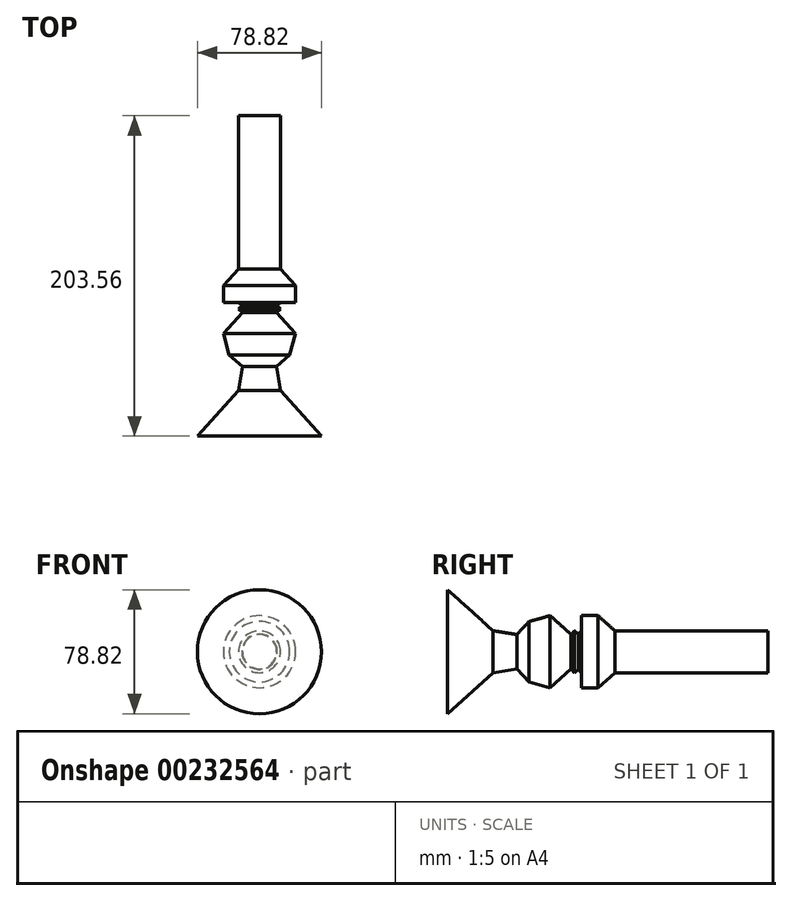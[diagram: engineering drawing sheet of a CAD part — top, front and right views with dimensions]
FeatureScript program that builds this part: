
annotation { "Feature Type Name" : "Feature", "Feature Type Description" : "" }
export const myFeature = defineFeature(function(context is Context, id is Id, definition is map)
    precondition{}
    {
        {
            var Q0;
            Q0=qCreatedBy(makeId("Top.planeOp"),FACE);
            var sketch = newSketch(context, id + "F0", { "sketchPlane" : qUnion([Q0])});
            skLineSegment(sketch, "E0", {"start": v(0, 54.64) * mm, "end": v(-13.33, 54.64) * mm});
            skLineSegment(sketch, "E1", {"start": v(-22.92, 43.98) * mm, "end": v(-13.33, 54.64) * mm});
            skLineSegment(sketch, "E2", {"start": v(-22.92, 43.98) * mm, "end": v(-22.92, 33.32) * mm});
            skLineSegment(sketch, "E3", {"start": v(-13.33, 33.32) * mm, "end": v(-11.2, 31.4) * mm});
            skLineSegment(sketch, "E4", {"start": v(-11.2, 31.4) * mm, "end": v(-13.33, 29.05) * mm});
            skLineSegment(sketch, "E5", {"start": v(-13.33, 29.05) * mm, "end": v(-10.91, 26.88) * mm});
            skLineSegment(sketch, "E6", {"start": v(-10.91, 26.88) * mm, "end": v(-13.33, 24.2) * mm});
            skLineSegment(sketch, "E7", {"start": v(-13.33, 24.2) * mm, "end": v(-22.92, 13.53) * mm});
            skLineSegment(sketch, "E8", {"start": v(-22.92, 13.53) * mm, "end": v(-19.2, 0) * mm});
            skLineSegment(sketch, "E9", {"start": v(-19.2, 0) * mm, "end": v(-10.91, -7.45) * mm});
            skLineSegment(sketch, "E10", {"start": v(-10.91, -7.45) * mm, "end": v(-13.33, -22.66) * mm});
            skLineSegment(sketch, "E11", {"start": v(-13.33, -22.66) * mm, "end": v(-22.92, -33.32) * mm});
            skLineSegment(sketch, "E12", {"start": v(-22.92, -33.32) * mm, "end": v(-39.4, -51.64) * mm});
            skLineSegment(sketch, "E13", {"start": v(-39.4, -51.64) * mm, "end": v(0, -51.64) * mm});
            skLineSegment(sketch, "E14", {"start": v(-22.92, 33.32) * mm, "end": v(-13.33, 33.32) * mm});
            skLineSegment(sketch, "E15", {"start": v(0, 54.64) * mm, "end": v(0, -51.64) * mm});
            skSolve(sketch);
        }
        {
            var Q0;
            Q0=makeQuery(id+"F0.imprint","IMPRINT",FACE,{"disambiguationData":[TD([[makeQuery(id+"F0.imprint","IMPRINT",EDGE,{"derivedFrom":sQuery(id+"F0.wireOp",EDGE,"E0")}),1.0]])]});
            var Q1;
            Q1=sQuery(id+"F0.wireOp",EDGE,"E15");
            revolve(context, id + "F1", {"entities" : qUnion([Q0]), "axis" : qUnion([Q1]), "revolveType" : RevolveType.FULL});
        }
        {
            var Q0;
            Q0=makeQuery(id+"F1.opRevolve","SWEPT_FACE",FACE,{"disambiguationData":[OSD([sQuery(id+"F0.wireOp",EDGE,"E0")])]});
            extrude(context, id + "F2", {"entities" : qUnion([Q0]), "operationType" : NewBodyOperationType.ADD, "depth" : 97.28 * mm});
        }
    });
